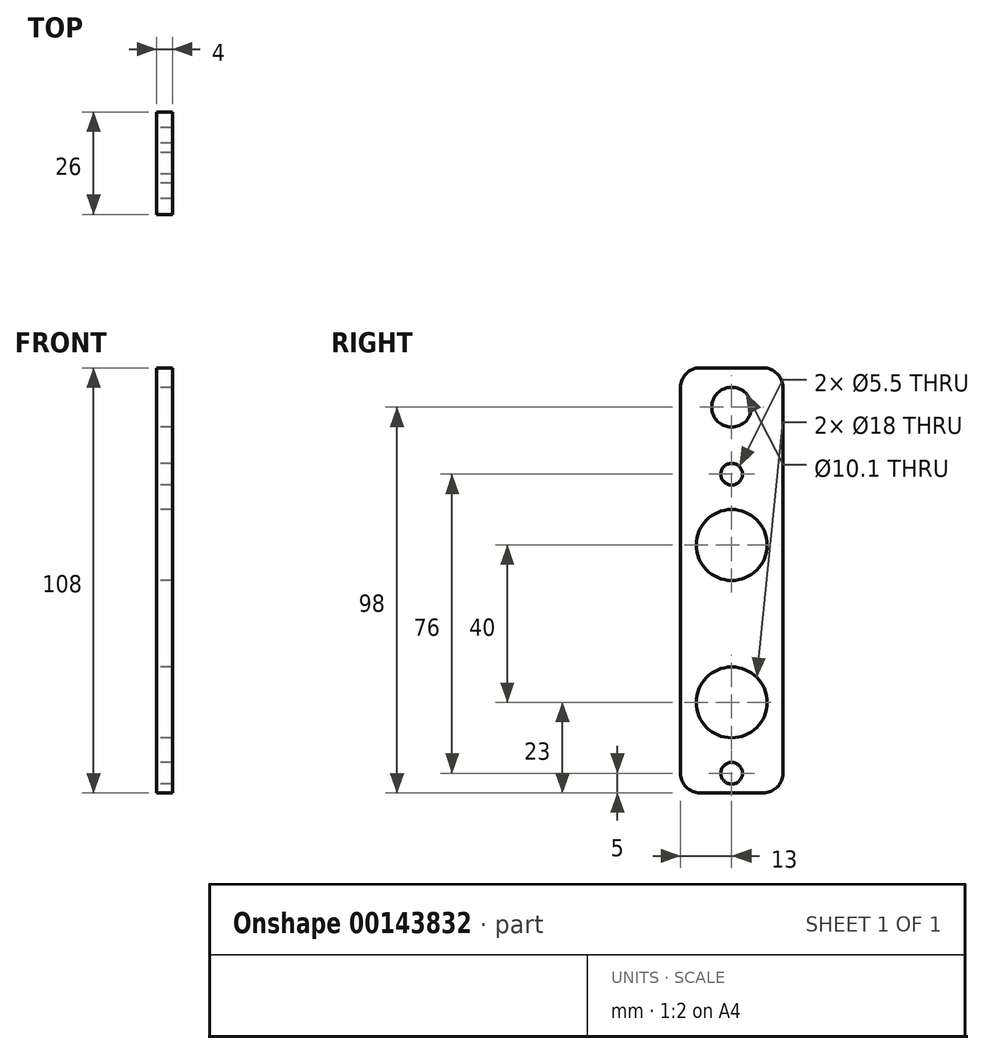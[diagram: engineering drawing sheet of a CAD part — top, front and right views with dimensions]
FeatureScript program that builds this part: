
annotation { "Feature Type Name" : "Feature", "Feature Type Description" : "" }
export const myFeature = defineFeature(function(context is Context, id is Id, definition is map)
    precondition{}
    {
        {
            var Q0;
            Q0=qCreatedBy(makeId("Right.planeOp"),FACE);
            var sketch = newSketch(context, id + "F0", { "sketchPlane" : qUnion([Q0])});
            skLineSegment(sketch, "E0.bottom", {"start": v(8, -54) * mm, "end": v(-8, -54) * mm});
            skLineSegment(sketch, "E0.top", {"start": v(8, 54) * mm, "end": v(-8, 54) * mm});
            skLineSegment(sketch, "E0.left", {"start": v(13, -49) * mm, "end": v(13, 49) * mm});
            skLineSegment(sketch, "E0.right", {"start": v(-13, -49) * mm, "end": v(-13, 49) * mm});
            skPoint(sketch, "E0.middle", {"position": v(0, 0) * mm});
            skCircle(sketch, "E1", {"center": v(0, 44) * mm, "radius": 5.05 * mm});
            skCircle(sketch, "E2", {"center": v(0, 27) * mm, "radius": 2.75 * mm});
            skCircle(sketch, "E3", {"center": v(0, 9) * mm, "radius": 9 * mm});
            skCircle(sketch, "E4", {"center": v(0, -31) * mm, "radius": 9 * mm});
            skCircle(sketch, "E5", {"center": v(0, -49) * mm, "radius": 2.75 * mm});
            skPoint(sketch, "E6.visualSharp", {"position": v(-13, 54) * mm});
            skArc(sketch, "E6.filletArc", {"start": v(-8, 54) * mm, "mid": v(-11.54, 52.54) * mm, "end": v(-13, 49) * mm});
            skPoint(sketch, "E7.visualSharp", {"position": v(13, 54) * mm});
            skArc(sketch, "E7.filletArc", {"start": v(13, 49) * mm, "mid": v(11.54, 52.54) * mm, "end": v(8, 54) * mm});
            skPoint(sketch, "E8.visualSharp", {"position": v(-13, -54) * mm});
            skArc(sketch, "E8.filletArc", {"start": v(-13, -49) * mm, "mid": v(-11.54, -52.54) * mm, "end": v(-8, -54) * mm});
            skPoint(sketch, "E9.visualSharp", {"position": v(13, -54) * mm});
            skArc(sketch, "E9.filletArc", {"start": v(8, -54) * mm, "mid": v(11.54, -52.54) * mm, "end": v(13, -49) * mm});
            skSolve(sketch);
        }
        {
            var Q0;
            Q0=makeQuery(id+"F0.imprint","IMPRINT",FACE,{"disambiguationData":[TD([[makeQuery(id+"F0.imprint","IMPRINT",EDGE,{"derivedFrom":sQuery(id+"F0.wireOp",EDGE,"E0.bottom")}),-1.0]])]});
            extrude(context, id + "F1", {"entities" : qUnion([Q0]), "depth" : 4 * mm});
        }
    });
